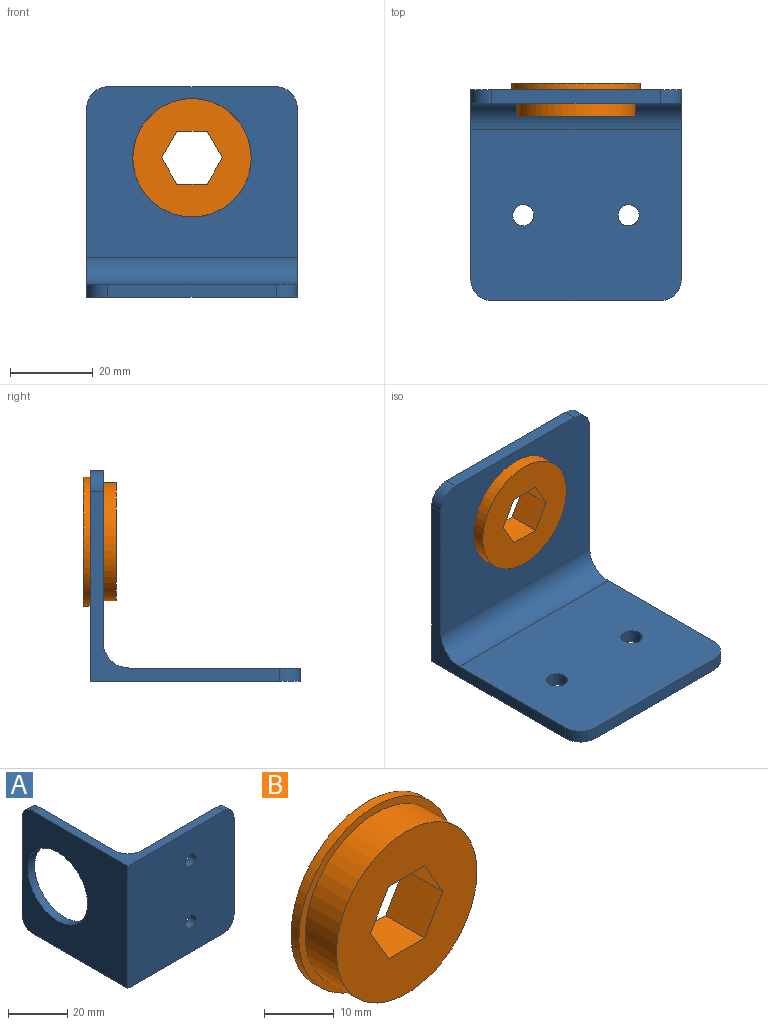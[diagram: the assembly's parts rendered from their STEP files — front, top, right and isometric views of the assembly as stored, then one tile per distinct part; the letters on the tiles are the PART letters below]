
ASSEMBLY  parts=2 mates=1
PART A: 16 faces, bbox 50.8x50.8x50.8 mm
  f0: cylinder r=6.35mm len=50.8mm, axis (0,0,-1), area 506.7mm2, adj f1,f6,f7,f8
  f1: plane 50.8x41.28mm, normal (1,0,0), area 1444.4mm2, adj f0,f2,f7,f8,f11,f13,f15
  f2: plane 40.64x3.18mm, normal (0,1,0), area 129mm2, adj f1,f3,f13,f15
  f3: plane 50.8x50.8mm, normal (-1,0,0), area 1928.3mm2, adj f2,f4,f7,f8,f11,f13,f15
  f4: plane 50.8x50.8mm, normal (0,-1,0), area 2528.6mm2, adj f3,f5,f7,f8,f9,f10,f12,f14
  f5: plane 40.64x3.18mm, normal (1,0,0), area 129mm2, adj f4,f6,f12,f14
  f6: plane 50.8x41.28mm, normal (0,1,0), area 2044.8mm2, adj f0,f5,f7,f8,f9,f10,f12,f14
  f7: plane 45.72x45.72mm, normal (0,0,1), area 288.9mm2, adj f0,f1,f3,f4,f6,f14,f15
  f8: plane 45.72x45.72mm, normal (0,0,-1), area 288.9mm2, adj f0,f1,f3,f4,f6,f12,f13
  f9: cylinder r=2.55mm len=5.11mm, axis (0,1,0), area 50.9mm2, adj f4,f6
  f10: cylinder r=2.55mm len=5.11mm, axis (0,1,0), area 50.9mm2, adj f4,f6
  f11: cylinder r=14.29mm len=28.58mm, axis (1,0,0), area 285mm2, adj f1,f3
  f12: cylinder r=5.08mm len=5.08mm, axis (0,1,0), area 25.3mm2, adj f4,f5,f6,f8
  f13: cylinder r=5.08mm len=5.08mm, axis (-1,0,0), area 25.3mm2, adj f1,f2,f3,f8
  f14: cylinder r=5.08mm len=5.08mm, axis (0,-1,0), area 25.3mm2, adj f4,f5,f6,f7
  f15: cylinder r=5.08mm len=5.08mm, axis (1,0,0), area 25.3mm2, adj f1,f2,f3,f7
PART B: 15 faces, bbox 31.1x7.9x31.1 mm
  f0: cylinder r=12.7mm len=25.4mm, axis (0,1,0), area 30.4mm2, adj f7,f8
  f1: cylinder r=15.56mm len=31.12mm, axis (0,1,0), area 155.2mm2, adj f6,f7
  f2: cylinder r=14.27mm len=28.55mm, axis (0,1,0), area 569.5mm2, adj f5,f6
  f3: cylinder r=9.53mm len=19.05mm, axis (0,1,0), area 22.8mm2, adj f4,f8
  f4: plane 19.05x19.05mm, normal (0,1,0), area 144.9mm2, adj f3,f9,f10,f11,f12,f13,f14
  f5: plane 28.55x28.55mm, normal (0,-1,0), area 500mm2, adj f2,f9,f10,f11,f12,f13,f14
  f6: plane 31.12x31.12mm, normal (0,-1,0), area 120.2mm2, adj f1,f2
  f7: plane 31.12x31.12mm, normal (0,1,0), area 253.7mm2, adj f0,f1
  f8: plane 25.4x25.4mm, normal (0,1,0), area 221.7mm2, adj f0,f3
  f9: plane 7.94x6.36mm, normal (-0.87,0,0.5), area 58.3mm2, adj f4,f5,f10,f14
  f10: plane 7.94x6.36mm, normal (-0.87,0,-0.5), area 58.3mm2, adj f4,f5,f9,f11
  f11: plane 7.94x7.34mm, normal (0,0,-1), area 58.3mm2, adj f4,f5,f10,f12
  f12: plane 7.94x6.36mm, normal (0.87,0,-0.5), area 58.3mm2, adj f4,f5,f11,f13
  f13: plane 7.94x6.36mm, normal (0.87,0,0.5), area 58.3mm2, adj f4,f5,f12,f14
  f14: plane 7.94x7.34mm, normal (0,0,1), area 58.3mm2, adj f4,f5,f9,f13
PLACE A rot(axis=(0.58,-0.58,-0.58),120deg) t=(25.4,35.49,-60.5)mm
PLACE B at identity
MATE revolute A.f11 <-> B.f0  axis (0,1,0) through (0,6.35,0)mm
